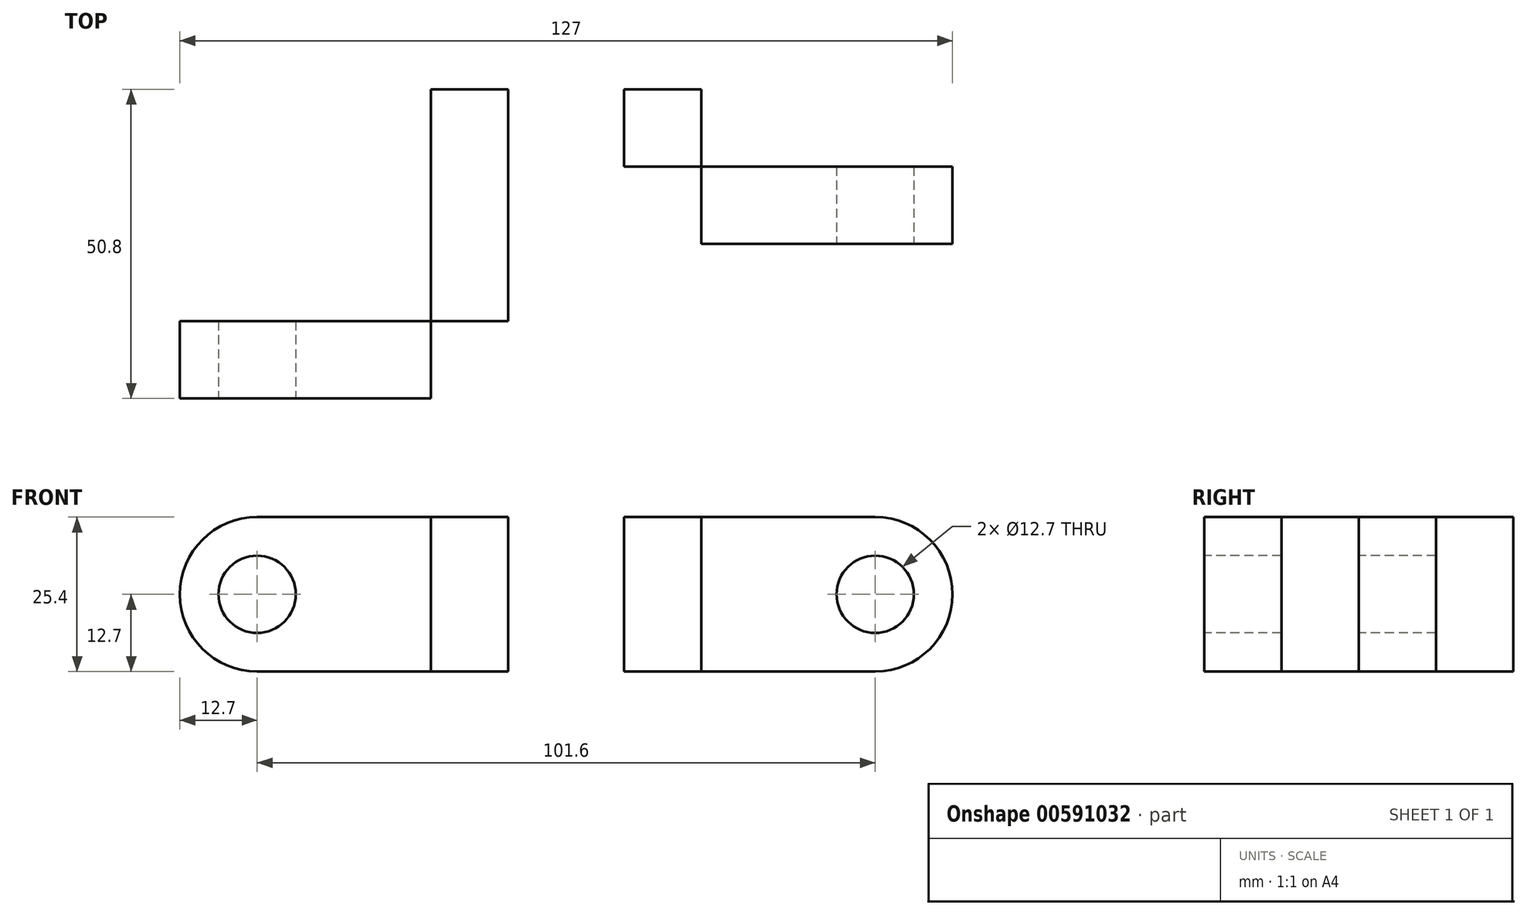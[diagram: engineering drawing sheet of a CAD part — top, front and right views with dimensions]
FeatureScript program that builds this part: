
annotation { "Feature Type Name" : "Feature", "Feature Type Description" : "" }
export const myFeature = defineFeature(function(context is Context, id is Id, definition is map)
    precondition{}
    {
        {
            var Q0;
            Q0=qCreatedBy(makeId("Top.planeOp"),FACE);
            var sketch = newSketch(context, id + "F0", { "sketchPlane" : qUnion([Q0])});
            skArc(sketch, "E0", {"start": v(-22.23, 0) * mm, "mid": v(0, 22.23) * mm, "end": v(22.23, 0) * mm});
            skArc(sketch, "E1.0", {"start": v(-9.53, 0) * mm, "mid": v(0, 9.53) * mm, "end": v(9.53, 0) * mm});
            skLineSegment(sketch, "E2.bottom", {"start": v(-9.53, 0) * mm, "end": v(-22.23, 0) * mm});
            skLineSegment(sketch, "E2.top", {"start": v(-9.52, -50.8) * mm, "end": v(-22.23, -50.8) * mm});
            skLineSegment(sketch, "E2.left", {"start": v(-9.53, 0) * mm, "end": v(-9.53, -50.8) * mm});
            skLineSegment(sketch, "E2.right", {"start": v(-22.23, 0) * mm, "end": v(-22.23, -50.8) * mm});
            skLineSegment(sketch, "E3.bottom", {"start": v(-9.52, -50.8) * mm, "end": v(-50.8, -50.8) * mm});
            skLineSegment(sketch, "E3.top", {"start": v(-9.52, -38.1) * mm, "end": v(-50.8, -38.1) * mm});
            skLineSegment(sketch, "E3.left", {"start": v(-9.52, -50.8) * mm, "end": v(-9.52, -38.1) * mm});
            skLineSegment(sketch, "E3.right", {"start": v(-50.8, -50.8) * mm, "end": v(-50.8, -38.1) * mm});
            skLineSegment(sketch, "E4.bottom", {"start": v(9.53, 0) * mm, "end": v(22.23, 0) * mm});
            skLineSegment(sketch, "E4.top", {"start": v(9.53, -25.4) * mm, "end": v(22.23, -25.4) * mm});
            skLineSegment(sketch, "E4.left", {"start": v(9.53, 0) * mm, "end": v(9.53, -25.4) * mm});
            skLineSegment(sketch, "E4.right", {"start": v(22.23, 0) * mm, "end": v(22.23, -25.4) * mm});
            skLineSegment(sketch, "E5.bottom", {"start": v(9.53, -25.4) * mm, "end": v(50.8, -25.4) * mm});
            skLineSegment(sketch, "E5.top", {"start": v(9.52, -12.7) * mm, "end": v(50.8, -12.7) * mm});
            skLineSegment(sketch, "E5.left", {"start": v(9.53, -25.4) * mm, "end": v(9.53, -12.7) * mm});
            skLineSegment(sketch, "E5.right", {"start": v(50.8, -25.4) * mm, "end": v(50.8, -12.7) * mm});
            skSolve(sketch);
        }
        {
            var Q0;
            {var subQ5=sQuery(id+"F0.wireOp",EDGE,"E3.right");Q0=makeQuery(id+"F0.imprint","IMPRINT",FACE,{"disambiguationData":[TD([[makeQuery(id+"F0.imprint","IMPRINT",EDGE,{"derivedFrom":subQ5}),-1.0]])]});}
            var Q1;
            {var subQ0=sQuery(id+"F0.wireOp",EDGE,"E2.bottom");Q1=makeQuery(id+"F0.imprint","IMPRINT",FACE,{"disambiguationData":[TD([[makeQuery(id+"F0.imprint","IMPRINT",EDGE,{"derivedFrom":subQ0}),1.0]])]});}
            var Q2;
            Q2=makeQuery(id+"F0.imprint","IMPRINT",FACE,{"disambiguationData":[TD([[makeQuery(id+"F0.imprint","IMPRINT",EDGE,{"derivedFrom":sQuery(id+"F0.wireOp",EDGE,"E0")}),-1.0]])]});
            var Q3;
            {var subQ0=sQuery(id+"F0.wireOp",EDGE,"E4.bottom");Q3=makeQuery(id+"F0.imprint","IMPRINT",FACE,{"disambiguationData":[TD([[makeQuery(id+"F0.imprint","IMPRINT",EDGE,{"derivedFrom":subQ0}),-1.0]])]});}
            var Q4;
            {var subQ5=sQuery(id+"F0.wireOp",EDGE,"E5.left");Q4=makeQuery(id+"F0.imprint","IMPRINT",FACE,{"disambiguationData":[TD([[makeQuery(id+"F0.imprint","IMPRINT",EDGE,{"derivedFrom":subQ5}),-1.0]])]});}
            var Q5;
            {var subQ5=sQuery(id+"F0.wireOp",EDGE,"E5.right");Q5=makeQuery(id+"F0.imprint","IMPRINT",FACE,{"disambiguationData":[TD([[makeQuery(id+"F0.imprint","IMPRINT",EDGE,{"derivedFrom":subQ5}),1.0]])]});}
            var Q6;
            {var subQ5=sQuery(id+"F0.wireOp",EDGE,"E3.left");Q6=makeQuery(id+"F0.imprint","IMPRINT",FACE,{"disambiguationData":[TD([[makeQuery(id+"F0.imprint","IMPRINT",EDGE,{"derivedFrom":subQ5}),1.0]])]});}
            extrude(context, id + "F1", {"entities" : qUnion([Q0, Q1, Q2, Q3, Q4, Q5, Q6]), "depth" : 25.4 * mm, "offsetDistance" : 25.4 * mm});
        }
        {
            var Q0;
            Q0=makeQuery(id+"F1.opExtrude","SWEPT_FACE",FACE,{"disambiguationData":[OSD([sQuery(id+"F0.wireOp",EDGE,"E3.right")])]});
            var sketch = newSketch(context, id + "F2", { "sketchPlane" : qUnion([Q0])});
            skLineSegment(sketch, "E6", {"start": v(38.1, 12.7) * mm, "end": v(50.8, 12.7) * mm});
            skSolve(sketch);
        }
        {
            var Q0;
            {var subQ0=sQuery(id+"F2.wireOp",EDGE,"E6");Q0=makeQuery(id+"F2.imprint","IMPRINT",FACE,{"disambiguationData":[TD([[makeQuery(id+"F2.imprint","IMPRINT",EDGE,{"derivedFrom":subQ0}),1.0]])]});}
            var Q1;
            Q1=sQuery(id+"F2.wireOp",EDGE,"E6");
            revolve(context, id + "F3", {"operationType" : NewBodyOperationType.ADD, "entities" : qUnion([Q0]), "axis" : qUnion([Q1]), "revolveType" : RevolveType.FULL});
        }
        {
            var Q0;
            Q0=makeQuery(id+"F1.opExtrude","SWEPT_FACE",FACE,{"disambiguationData":[OSD([sQuery(id+"F0.wireOp",EDGE,"E5.right")])]});
            var sketch = newSketch(context, id + "F4", { "sketchPlane" : qUnion([Q0])});
            skLineSegment(sketch, "E7", {"start": v(-25.4, 12.7) * mm, "end": v(-12.7, 12.7) * mm});
            skSolve(sketch);
        }
        {
            var Q0;
            {var subQ0=sQuery(id+"F4.wireOp",EDGE,"E7");Q0=makeQuery(id+"F4.imprint","IMPRINT",FACE,{"disambiguationData":[TD([[makeQuery(id+"F4.imprint","IMPRINT",EDGE,{"derivedFrom":subQ0}),1.0]])]});}
            var Q1;
            Q1=sQuery(id+"F4.wireOp",EDGE,"E7");
            revolve(context, id + "F5", {"operationType" : NewBodyOperationType.ADD, "entities" : qUnion([Q0]), "axis" : qUnion([Q1]), "revolveType" : RevolveType.FULL});
        }
        {
            var Q0;
            {var subQ0=sQuery(id+"F0.wireOp",EDGE,"E5.bottom");Q0=makeQuery(id+"F5.boolean.opBoolean","MERGE",FACE,{"derivedFrom":[makeQuery(id+"F1.opExtrude","SWEPT_FACE",FACE,{"disambiguationData":[OSD([subQ0])]}),makeQuery(id+"F5.opRevolve","SWEPT_FACE",FACE,{"disambiguationData":[OSD([subQ0,sQuery(id+"F0.wireOp",EDGE,"E5.right")])]})]});}
            var sketch = newSketch(context, id + "F6", { "sketchPlane" : qUnion([Q0])});
            skLineSegment(sketch, "E8", {"start": v(50.8, 25.4) * mm, "end": v(50.8, 0) * mm});
            skCircle(sketch, "E9", {"center": v(50.8, 12.7) * mm, "radius": 6.35 * mm});
            skSolve(sketch);
        }
        {
            var Q0;
            Q0 = qSketchRegion(id + "F6", true);
            extrude(context, id + "F7", {"entities" : qUnion([Q0]), "operationType" : NewBodyOperationType.REMOVE, "oppositeDirection" : true, "depth" : 25.4 * mm, "offsetDistance" : 25.4 * mm});
        }
        {
            var Q0;
            {var subQ0=sQuery(id+"F0.wireOp",EDGE,"E3.bottom");Q0=makeQuery(id+"F3.boolean.opBoolean","MERGE",FACE,{"derivedFrom":[makeQuery(id+"F1.opExtrude","SWEPT_FACE",FACE,{"disambiguationData":[OSD([subQ0])]}),makeQuery(id+"F3.opRevolve","SWEPT_FACE",FACE,{"disambiguationData":[OSD([subQ0,sQuery(id+"F0.wireOp",EDGE,"E3.right")])]})]});}
            var sketch = newSketch(context, id + "F8", { "sketchPlane" : qUnion([Q0])});
            skLineSegment(sketch, "E10", {"start": v(-50.8, 25.4) * mm, "end": v(-50.8, 0) * mm});
            skCircle(sketch, "E11", {"center": v(-50.8, 12.7) * mm, "radius": 6.35 * mm});
            skSolve(sketch);
        }
        {
            var Q0;
            Q0 = qSketchRegion(id + "F8", true);
            extrude(context, id + "F9", {"entities" : qUnion([Q0]), "operationType" : NewBodyOperationType.REMOVE, "oppositeDirection" : true, "depth" : 25.4 * mm, "offsetDistance" : 25.4 * mm});
        }
    });
